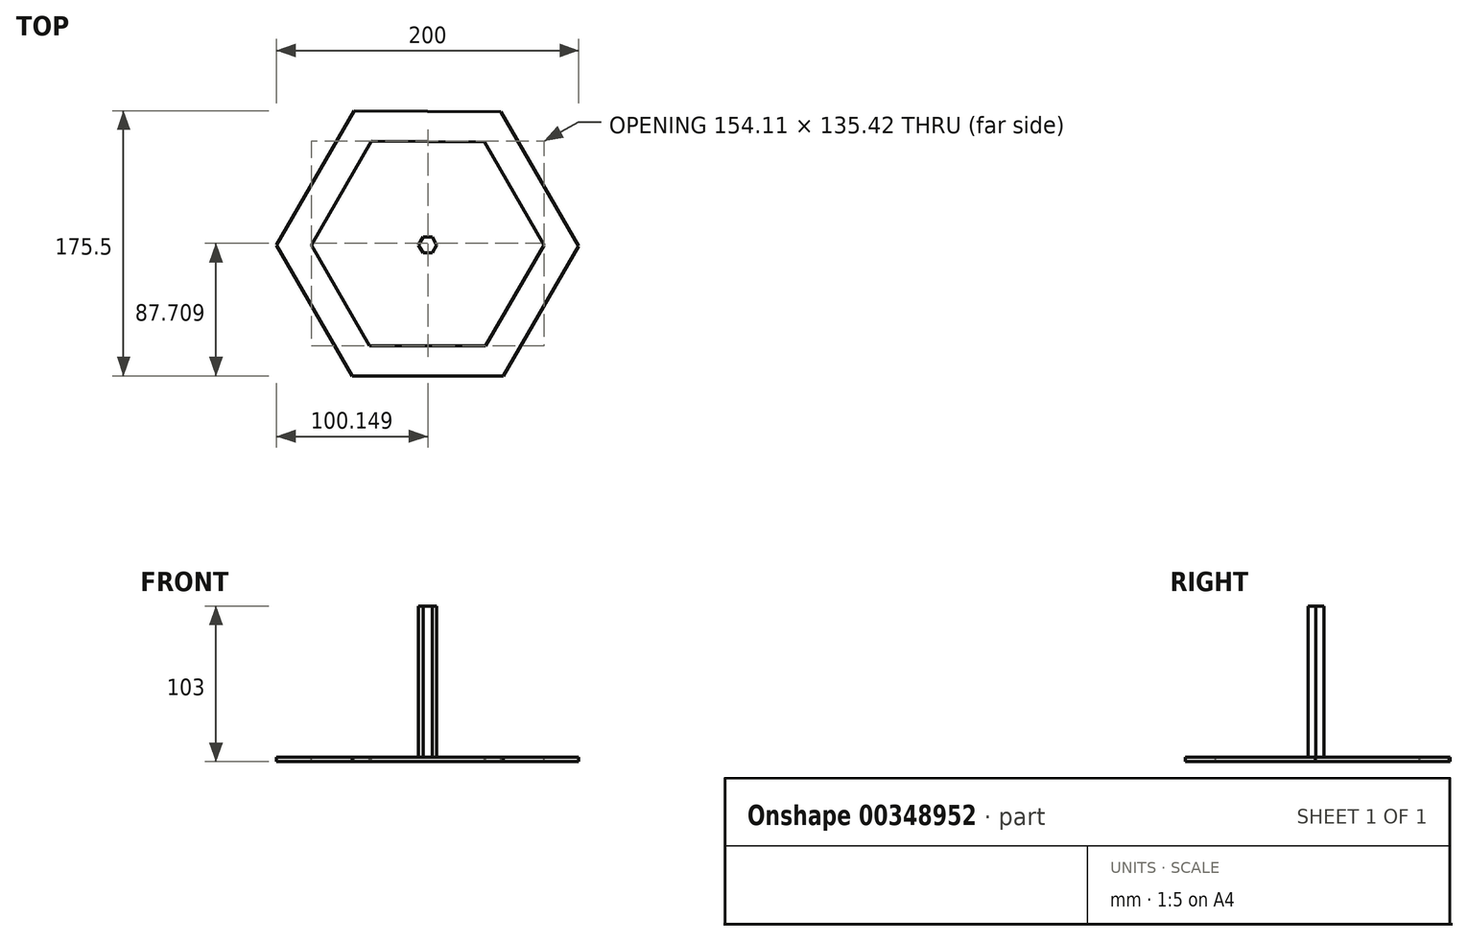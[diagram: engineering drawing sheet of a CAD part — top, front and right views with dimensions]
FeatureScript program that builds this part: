
annotation { "Feature Type Name" : "Feature", "Feature Type Description" : "" }
export const myFeature = defineFeature(function(context is Context, id is Id, definition is map)
    precondition{}
    {
        {
            var Q0;
            Q0=qCreatedBy(makeId("Top.planeOp"),FACE);
            var sketch = newSketch(context, id + "F0", { "sketchPlane" : qUnion([Q0])});
            skLineSegment(sketch, "E0.0", {"start": v(-48.67, 88.9) * mm, "end": v(48.67, 88.22) * mm});
            skLineSegment(sketch, "E0.1", {"start": v(48.67, 88.22) * mm, "end": v(100, -0.59) * mm});
            skLineSegment(sketch, "E0.2", {"start": v(100, -0.59) * mm, "end": v(49.96, -86.6) * mm});
            skLineSegment(sketch, "E0.3", {"start": v(49.96, -86.6) * mm, "end": v(-50, -86.6) * mm});
            skLineSegment(sketch, "E0.4", {"start": v(-50, -86.6) * mm, "end": v(-100, 0) * mm});
            skLineSegment(sketch, "E0.5", {"start": v(-100, 0) * mm, "end": v(-48.67, 88.9) * mm});
            skPoint(sketch, "E0.0.midPoint", {"position": v(0, 88.56) * mm});
            skCircle(sketch, "E1.cCircle", {"center": v(0, 0) * mm, "radius": 5.2 * mm, "construction": true});
            skLineSegment(sketch, "E1.0", {"start": v(-3, 5.2) * mm, "end": v(3, 5.2) * mm});
            skLineSegment(sketch, "E1.1", {"start": v(3, 5.2) * mm, "end": v(6, 0) * mm});
            skLineSegment(sketch, "E1.2", {"start": v(6, 0) * mm, "end": v(3, -5.2) * mm});
            skLineSegment(sketch, "E1.3", {"start": v(3, -5.2) * mm, "end": v(-3, -5.2) * mm});
            skLineSegment(sketch, "E1.4", {"start": v(-3, -5.2) * mm, "end": v(-6, 0) * mm});
            skLineSegment(sketch, "E1.5", {"start": v(-6, 0) * mm, "end": v(-3, 5.2) * mm});
            skPoint(sketch, "E1.0.midPoint", {"position": v(0, 5.2) * mm});
            skLineSegment(sketch, "E2", {"start": v(-100, 0) * mm, "end": v(-6, 0) * mm});
            skLineSegment(sketch, "E3", {"start": v(-48.67, 88.9) * mm, "end": v(-3, 5.2) * mm});
            skLineSegment(sketch, "E4", {"start": v(48.67, 88.22) * mm, "end": v(3, 5.2) * mm});
            skLineSegment(sketch, "E5", {"start": v(100, -0.59) * mm, "end": v(6, 0) * mm});
            skLineSegment(sketch, "E6", {"start": v(-50, -86.6) * mm, "end": v(-3, -5.2) * mm});
            skLineSegment(sketch, "E7", {"start": v(49.96, -86.6) * mm, "end": v(3, -5.2) * mm});
            skPoint(sketch, "E8.cCircle.perimeterSnap0", {"position": v(0, -5.2) * mm});
            skLineSegment(sketch, "E8.0", {"start": v(27.2, -47.6) * mm, "end": v(-27.2, -47.6) * mm});
            skLineSegment(sketch, "E8.1", {"start": v(-27.2, -47.6) * mm, "end": v(-54.83, 0.25) * mm});
            skLineSegment(sketch, "E8.2", {"start": v(-54.83, 0.25) * mm, "end": v(-26.92, 48.58) * mm});
            skLineSegment(sketch, "E8.3", {"start": v(-26.92, 48.58) * mm, "end": v(26.66, 48.2) * mm});
            skLineSegment(sketch, "E8.4", {"start": v(26.66, 48.2) * mm, "end": v(54.7, -0.32) * mm});
            skLineSegment(sketch, "E8.5", {"start": v(54.7, -0.32) * mm, "end": v(27.2, -47.6) * mm});
            skPoint(sketch, "E8.0.midPoint", {"position": v(0, -47.6) * mm});
            skPoint(sketch, "E8.0.midPoint.positionSnap0", {"position": v(0, -5.2) * mm});
            skLineSegment(sketch, "E9.0", {"start": v(38.45, -66.6) * mm, "end": v(-38.45, -66.6) * mm});
            skLineSegment(sketch, "E9.1", {"start": v(-38.45, -66.6) * mm, "end": v(-76.9, 0) * mm});
            skLineSegment(sketch, "E9.2", {"start": v(-76.9, 0) * mm, "end": v(-37.17, 68.82) * mm});
            skLineSegment(sketch, "E9.3", {"start": v(-37.17, 68.82) * mm, "end": v(37.73, 68.3) * mm});
            skLineSegment(sketch, "E9.4", {"start": v(37.73, 68.3) * mm, "end": v(77.2, 0) * mm});
            skLineSegment(sketch, "E9.5", {"start": v(77.2, 0) * mm, "end": v(38.45, -66.6) * mm});
            skPoint(sketch, "E9.0.midPoint", {"position": v(0, -66.6) * mm});
            skSolve(sketch);
        }
        {
            var Q0;
            Q0=makeQuery(id+"F0.imprint","IMPRINT",FACE,{"disambiguationData":[TD([[makeQuery(id+"F0.imprint","IMPRINT",EDGE,{"derivedFrom":sQuery(id+"F0.wireOp",EDGE,"E1.0")}),-1.0]])]});
            extrude(context, id + "F1", {"entities" : qUnion([Q0]), "depth" : 100 * mm});
        }
        {
            var Q0;
            Q0 = qSketchRegion(id + "F0", true);
            extrude(context, id + "F2", {"entities" : qUnion([Q0]), "depth" : -3 * mm});
        }
    });
